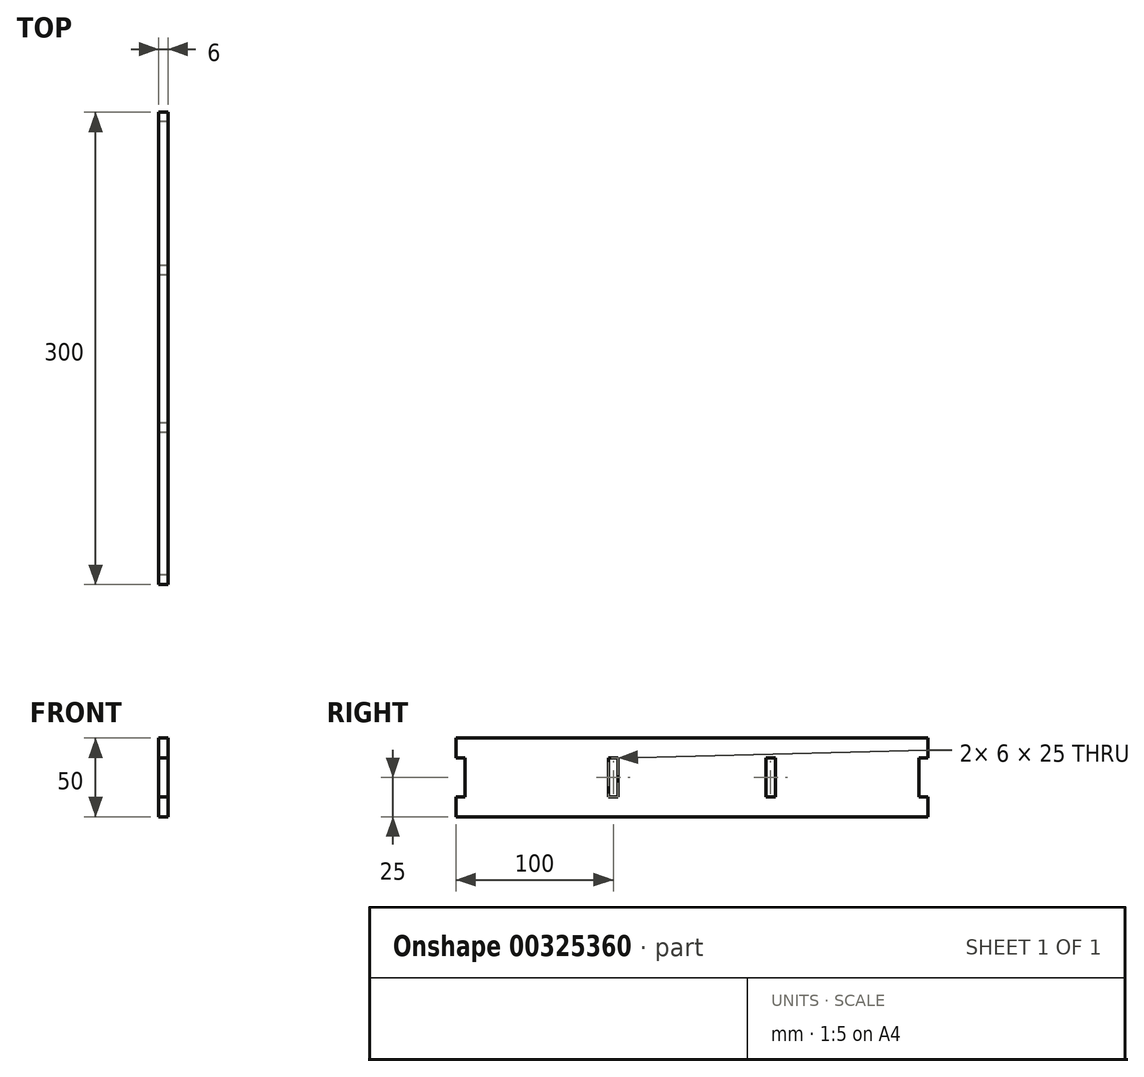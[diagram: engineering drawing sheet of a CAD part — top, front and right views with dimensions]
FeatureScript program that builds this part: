
annotation { "Feature Type Name" : "Feature", "Feature Type Description" : "" }
export const myFeature = defineFeature(function(context is Context, id is Id, definition is map)
    precondition{}
    {
        {
            var Q0;
            Q0=qCreatedBy(makeId("Right.planeOp"),FACE);
            var sketch = newSketch(context, id + "F0", { "sketchPlane" : qUnion([Q0])});
            skLineSegment(sketch, "E0.bottom", {"start": v(-150, 25) * mm, "end": v(150, 25) * mm});
            skLineSegment(sketch, "E0.top", {"start": v(-150, -25) * mm, "end": v(150, -25) * mm});
            skLineSegment(sketch, "E0.left", {"start": v(-150, 25) * mm, "end": v(-150, -25) * mm});
            skLineSegment(sketch, "E0.right", {"start": v(150, 25) * mm, "end": v(150, -25) * mm});
            skPoint(sketch, "E0.middle", {"position": v(0, 0) * mm});
            skLineSegment(sketch, "E1.bottom", {"start": v(-75, 25) * mm, "end": v(75, 25) * mm});
            skLineSegment(sketch, "E1.top", {"start": v(-75, 19) * mm, "end": v(75, 19) * mm});
            skLineSegment(sketch, "E1.left", {"start": v(-75, 25) * mm, "end": v(-75, 19) * mm});
            skLineSegment(sketch, "E1.right", {"start": v(75, 25) * mm, "end": v(75, 19) * mm});
            skPoint(sketch, "E1.middle", {"position": v(0, 22) * mm});
            skLineSegment(sketch, "E2.bottom", {"start": v(-150, 12.5) * mm, "end": v(-144, 12.5) * mm});
            skLineSegment(sketch, "E2.top", {"start": v(-150, -12.5) * mm, "end": v(-144, -12.5) * mm});
            skLineSegment(sketch, "E2.left", {"start": v(-150, 12.5) * mm, "end": v(-150, -12.5) * mm});
            skLineSegment(sketch, "E2.right", {"start": v(-144, 12.5) * mm, "end": v(-144, -12.5) * mm});
            skPoint(sketch, "E2.middle", {"position": v(-147, 0) * mm});
            skLineSegment(sketch, "E3.bottom", {"start": v(150, 12.5) * mm, "end": v(144, 12.5) * mm});
            skLineSegment(sketch, "E3.top", {"start": v(150, -12.5) * mm, "end": v(144, -12.5) * mm});
            skLineSegment(sketch, "E3.left", {"start": v(150, 12.5) * mm, "end": v(150, -12.5) * mm});
            skLineSegment(sketch, "E3.right", {"start": v(144, 12.5) * mm, "end": v(144, -12.5) * mm});
            skPoint(sketch, "E3.middle", {"position": v(147, 0) * mm});
            skPoint(sketch, "E3.middle.positionSnap0", {"position": v(150, 0) * mm});
            skPoint(sketch, "E3.centerSnap0", {"position": v(150, 0) * mm});
            skLineSegment(sketch, "E4.bottom", {"start": v(-75, -25) * mm, "end": v(75, -25) * mm});
            skLineSegment(sketch, "E4.top", {"start": v(-75, -19) * mm, "end": v(75, -19) * mm});
            skLineSegment(sketch, "E4.left", {"start": v(-75, -25) * mm, "end": v(-75, -19) * mm});
            skLineSegment(sketch, "E4.right", {"start": v(75, -25) * mm, "end": v(75, -19) * mm});
            skPoint(sketch, "E4.middle", {"position": v(0, -22) * mm});
            skLineSegment(sketch, "E5.top", {"start": v(-75, 31) * mm, "end": v(75, 31) * mm});
            skLineSegment(sketch, "E5.left", {"start": v(-75, 25) * mm, "end": v(-75, 31) * mm});
            skLineSegment(sketch, "E5.right", {"start": v(75, 25) * mm, "end": v(75, 31) * mm});
            skLineSegment(sketch, "E6.top", {"start": v(-75, -31) * mm, "end": v(75, -31) * mm});
            skLineSegment(sketch, "E6.left", {"start": v(-75, -25) * mm, "end": v(-75, -31) * mm});
            skLineSegment(sketch, "E6.right", {"start": v(75, -25) * mm, "end": v(75, -31) * mm});
            skSolve(sketch);
        }
        {
            var Q0;
            Q0=makeQuery(id+"F0.imprint","IMPRINT",FACE,{"disambiguationData":[TD([[makeQuery(id+"F0.imprint","IMPRINT",EDGE,{"derivedFrom":sQuery(id+"F0.wireOp",EDGE,"E1.top")}),-1.0]])]});
            var Q1;
            Q1=makeQuery(id+"F0.imprint","IMPRINT",FACE,{"disambiguationData":[TD([[makeQuery(id+"F0.imprint","IMPRINT",EDGE,{"derivedFrom":sQuery(id+"F0.wireOp",EDGE,"E1.bottom")}),1.0]])]});
            var Q2;
            Q2=makeQuery(id+"F0.imprint","IMPRINT",FACE,{"disambiguationData":[TD([[makeQuery(id+"F0.imprint","IMPRINT",EDGE,{"derivedFrom":sQuery(id+"F0.wireOp",EDGE,"E1.top")}),1.0]])]});
            var Q3;
            Q3=makeQuery(id+"F0.imprint","IMPRINT",FACE,{"disambiguationData":[TD([[makeQuery(id+"F0.imprint","IMPRINT",EDGE,{"derivedFrom":sQuery(id+"F0.wireOp",EDGE,"E4.bottom")}),-1.0]])]});
            var Q4;
            Q4=makeQuery(id+"F0.imprint","IMPRINT",FACE,{"disambiguationData":[TD([[makeQuery(id+"F0.imprint","IMPRINT",EDGE,{"derivedFrom":sQuery(id+"F0.wireOp",EDGE,"E4.top")}),-1.0]])]});
            extrude(context, id + "F1", {"entities" : qUnion([Q0, Q1, Q2, Q3, Q4]), "depth" : 6 * mm});
        }
        {
            var Q0;
            Q0=makeQuery(id+"F1.opExtrude","CAP_FACE",FACE,{"disambiguationData":[OSD([sQuery(id+"F0.wireOp",EDGE,"E0.bottom"),sQuery(id+"F0.wireOp",EDGE,"E0.top"),sQuery(id+"F0.wireOp",EDGE,"E0.left"),sQuery(id+"F0.wireOp",EDGE,"E0.right"),sQuery(id+"F0.wireOp",EDGE,"E2.bottom"),sQuery(id+"F0.wireOp",EDGE,"E2.top"),sQuery(id+"F0.wireOp",EDGE,"E2.right"),sQuery(id+"F0.wireOp",EDGE,"E3.bottom"),sQuery(id+"F0.wireOp",EDGE,"E3.top"),sQuery(id+"F0.wireOp",EDGE,"E3.right"),sQuery(id+"F0.wireOp",EDGE,"E5.top"),sQuery(id+"F0.wireOp",EDGE,"E5.left"),sQuery(id+"F0.wireOp",EDGE,"E5.right"),sQuery(id+"F0.wireOp",EDGE,"E6.top"),sQuery(id+"F0.wireOp",EDGE,"E6.left"),sQuery(id+"F0.wireOp",EDGE,"E6.right")])],"isStart":false});
            var sketch = newSketch(context, id + "F2", { "sketchPlane" : qUnion([Q0])});
            skLineSegment(sketch, "E7.bottom", {"start": v(-53, 12.5) * mm, "end": v(-47, 12.5) * mm});
            skLineSegment(sketch, "E7.top", {"start": v(-53, -12.5) * mm, "end": v(-47, -12.5) * mm});
            skLineSegment(sketch, "E7.left", {"start": v(-53, 12.5) * mm, "end": v(-53, -12.5) * mm});
            skLineSegment(sketch, "E7.right", {"start": v(-47, 12.5) * mm, "end": v(-47, -12.5) * mm});
            skPoint(sketch, "E7.middle", {"position": v(-50, 0) * mm});
            skLineSegment(sketch, "E8", {"start": v(0, 31) * mm, "end": v(0, -31) * mm});
            skLineSegment(sketch, "E9.MirrorCS", {"start": v(53, -12.5) * mm, "end": v(47, -12.5) * mm});
            skLineSegment(sketch, "E10.MirrorCS", {"start": v(53, 12.5) * mm, "end": v(53, -12.5) * mm});
            skLineSegment(sketch, "E11.MirrorCS", {"start": v(47, 12.5) * mm, "end": v(47, -12.5) * mm});
            skLineSegment(sketch, "E12.MirrorCS", {"start": v(53, 12.5) * mm, "end": v(47, 12.5) * mm});
            skSolve(sketch);
        }
        {
            var Q0;
            Q0=qSketchRegion(id+"F2",true);
            extrude(context, id + "F3", {"entities" : qUnion([Q0]), "operationType" : NewBodyOperationType.REMOVE, "endBound" : BoundingType.UP_TO_NEXT, "oppositeDirection" : true, "depth" : 25 * mm});
        }
    });
